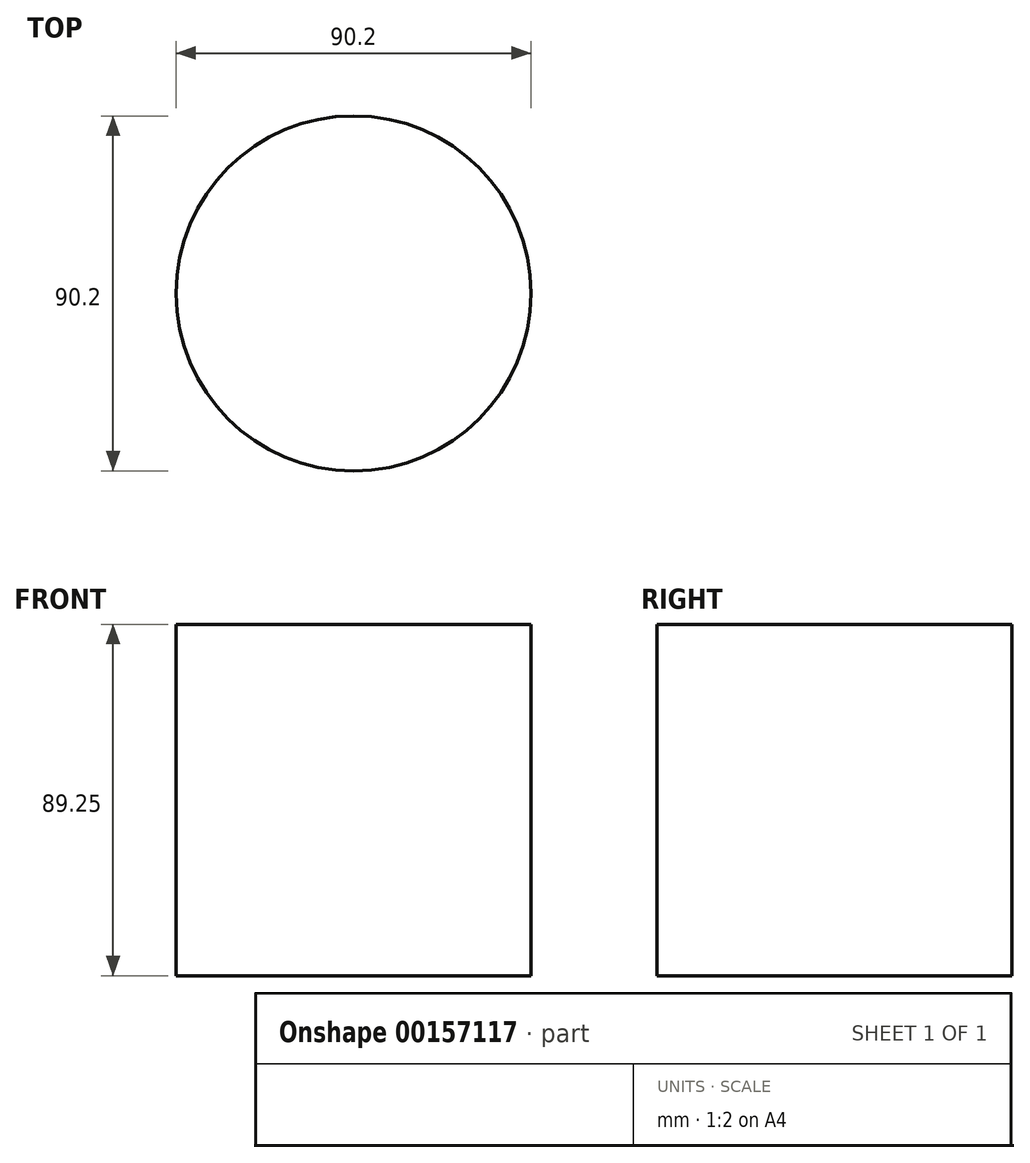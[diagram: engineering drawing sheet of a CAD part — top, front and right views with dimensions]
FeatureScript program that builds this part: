
annotation { "Feature Type Name" : "Feature", "Feature Type Description" : "" }
export const myFeature = defineFeature(function(context is Context, id is Id, definition is map)
    precondition{}
    {
        {
            var Q0;
            Q0=qCreatedBy(makeId("Top.planeOp"),FACE);
            var sketch = newSketch(context, id + "F0", { "sketchPlane" : qUnion([Q0])});
            skCircle(sketch, "E0", {"center": v(0, 0) * mm, "radius": 45.1 * mm});
            skSolve(sketch);
        }
        {
            var Q0;
            Q0=makeQuery(id+"F0.imprint","IMPRINT",FACE,{"disambiguationData":[TD([[makeQuery(id+"F0.imprint","IMPRINT",EDGE,{"derivedFrom":sQuery(id+"F0.wireOp",EDGE,"E0")}),1.0]])]});
            var Q1;
            Q1=sQuery(id+"F0.wireOp",EDGE,"E0");
            extrude(context, id + "F1", {"entities" : qUnion([Q0]), "surfaceEntities" : qUnion([Q1]), "depth" : 89.25 * mm});
        }
    });
